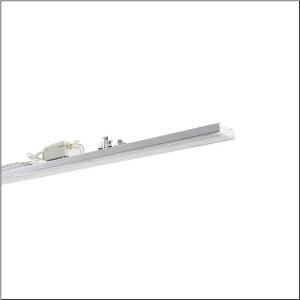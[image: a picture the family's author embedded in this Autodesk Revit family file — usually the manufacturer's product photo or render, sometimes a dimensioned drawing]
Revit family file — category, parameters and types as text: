
# Revit family: licross_11_recessed_mo_51te1e7n485g
name_source: partatom
category: Lighting Fixtures
units: mm (PartAtom-declared; Revit-internal decimal feet)

## family parameters
Cut with Voids When Loaded = No
Host = Face
Light Source = No
Part Type = Normal
Room Calculation Point = No
Round Connector Dimension = Use Diameter
Shared = No

## types (1)
- Licross 11 Recessed MO (1 x LED, 8660 lm, 48.5 W, 4000K)
    Apparent Load = 49 VA
    CIE Flux Codes = 85 95 99 100 100
    Color Rendering = 80
    Color Temperature = 4000K
    Default Elevation = 1800 mm
    Description = Licross 11 Recessed MO, luminaire insert, of sheet steel, galvanised, coil coated, white, length: 1.500mm, width: 66mm, height: 67mm, LED rated luminous flux: 8.660lm, light colour: 840, SDCM (Standard Deviation of Colour Matching)MacAdam ≤ 2 SDCM (initial), control gear: ON/OFF, with plug, 3-pole, with phase selection, mains connection: 220..240V, AC, 50/60Hz, rated input power: 49W, internal wiring halogen-free, primary light control with lens, of plastic, primary optical cover: cover, of PMMA, light emission: direct distribution, primary light characteristic: symmetric, protection rating (complete): IP54, insulation class (complete): insulation class I (protective earthing), certification: CE, ENEC, VDE, UKCA, protection symbol: D if used in an environment with non-conductive dust loads with corresponding accessories, impact resistance: IK06, permissible ambient temperature for indoor applications: -35..+35°C, corresponds to IFS (International Featured Standards) requirements for safety and quality in the food industry, reducing of maximum allowable ambient temperature of 5°C with ceiling mounting, The light source and the operating device comply with the requirements of the Ecodesign Regulation (EU) 2019/2020 and are replaceable in accordance with this regulation, packaging unit: 1 piece
    Height = 58 mm
    Lamp = 1 x LED
    Lamp Light Flux = 8660 lm
    Lamp Power = 48.5 W
    Lamp count = 1
    Length = 1500 mm
    Luminous efficacy = 179 lm/W
    Manufacturer = Siteco
    ModVariant = No
    Model = 51TE1E7N485G
    Mounting Place = Ceiling
    Mounting Type = Pendant
    Number of Poles = 1
    OnlyDefault = Yes
    Power Factor = 1
    Product Name = Licross 11 Recessed MO
    Product group = luminaire insert | ceiling pendant
    ProductGroupID = 901
    Protection Class = Protection class I
    Protection Degree = IP 54
    RLX_Detail_Level = 1
    RLX_Emergency_Light_Flux = 0 lm
    RLX_Emergency_Type = 0
    RLX_Emergency_Type_DB = No
    RlxData = <blob elided: 21189 chars, md5=8d323106>
    Socket = socket
    Standby Power = 0 W
    System Light Flux = 8660 lm
    System Power = 49 W
    Type Comments = Product without accessories
    Type Image = l_1296930.jpg
    URL = http://relux.com
    VarID = ---
    Voltage = 0 V
    Weight = 0.00 kg
    Width = 66 mm

## geometry (parser evidence)
native form markers: Blend x4, Sweep x11
no freeform markers — native parametric forms only
